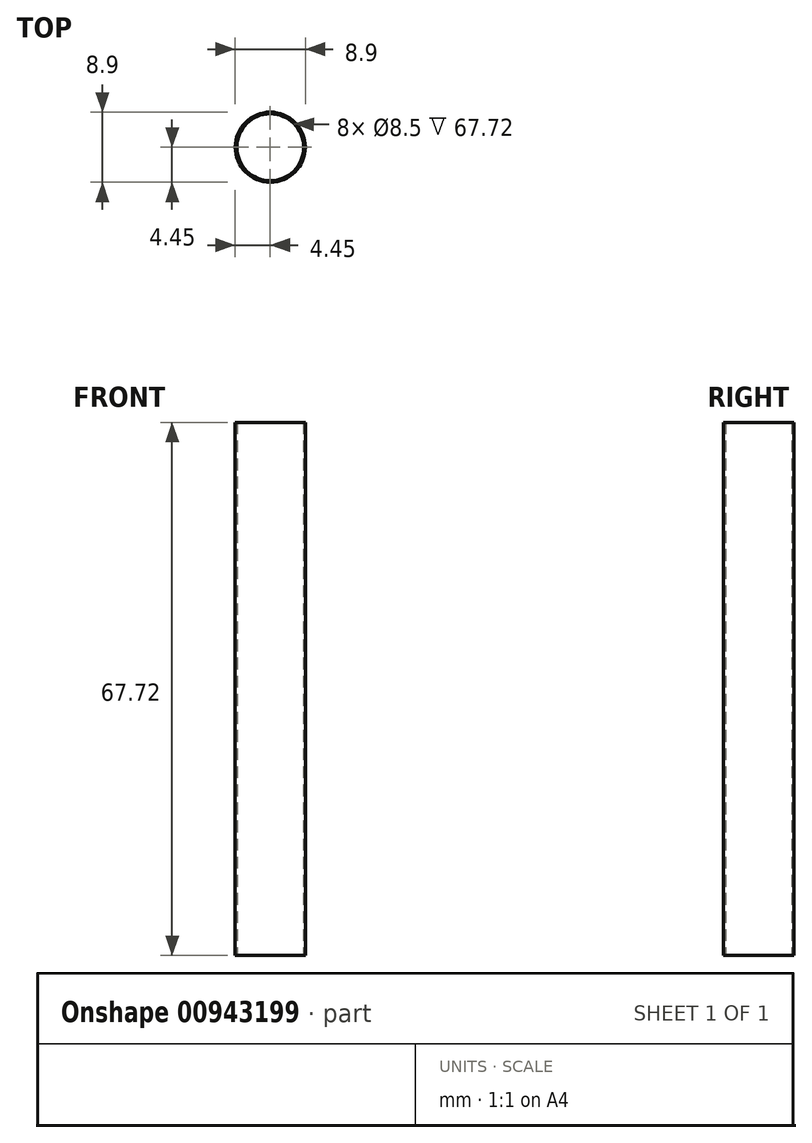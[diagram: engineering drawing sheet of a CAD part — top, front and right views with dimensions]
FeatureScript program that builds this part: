
annotation { "Feature Type Name" : "Feature", "Feature Type Description" : "" }
export const myFeature = defineFeature(function(context is Context, id is Id, definition is map)
    precondition{}
    {
        {
            var Q0;
            Q0=qCreatedBy(makeId("Top.planeOp"),FACE);
            var sketch = newSketch(context, id + "F0", { "sketchPlane" : qUnion([Q0])});
            skCircle(sketch, "E0", {"center": v(0, 0) * mm, "radius": 4.25 * mm});
            skCircle(sketch, "E1", {"center": v(0, 0) * mm, "radius": 4.45 * mm});
            skSolve(sketch);
        }
        {
            var Q0;
            Q0=qSketchRegion(id+"F0",true);
            var Q1;
            Q1=qConstructionFilter(qBodyType(qCreatedBy(id+"F0",EDGE),BodyType.WIRE),ConstructionObject.NO);
            extrude(context, id + "F1", {"entities" : qUnion([Q0]), "surfaceEntities" : qUnion([Q1]), "depth" : 67.72 * mm, "offsetDistance" : 25 * mm});
        }
    });
